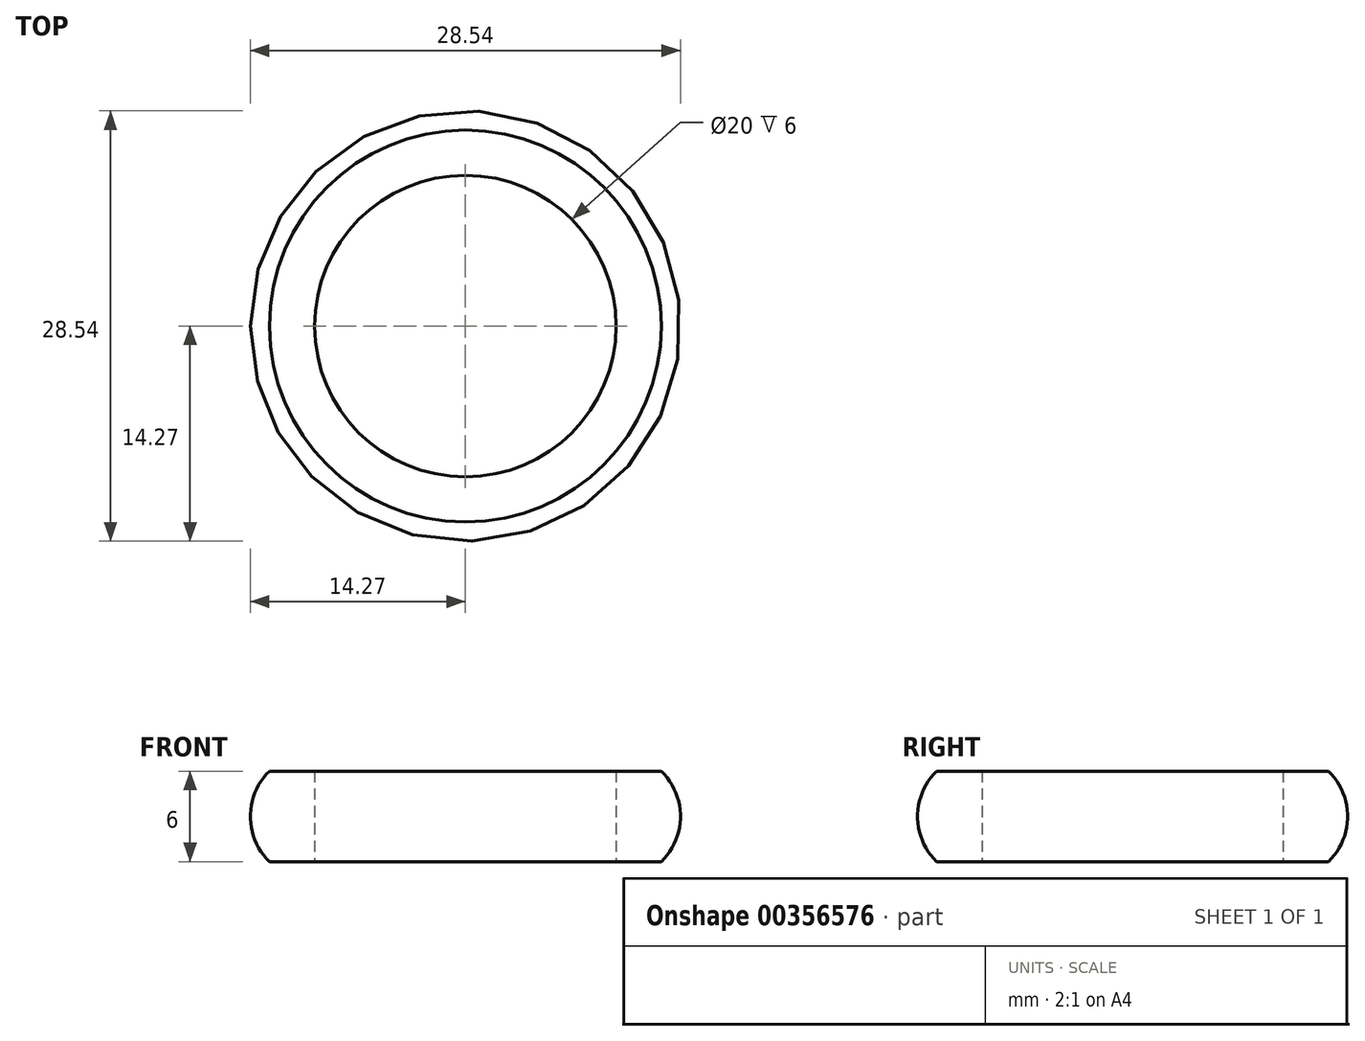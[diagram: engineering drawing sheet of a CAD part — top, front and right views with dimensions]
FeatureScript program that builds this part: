
annotation { "Feature Type Name" : "Feature", "Feature Type Description" : "" }
export const myFeature = defineFeature(function(context is Context, id is Id, definition is map)
    precondition{}
    {
        {
            var Q0;
            Q0=qCreatedBy(makeId("Front.planeOp"),FACE);
            var sketch = newSketch(context, id + "F0", { "sketchPlane" : qUnion([Q0])});
            skLineSegment(sketch, "E0", {"start": v(0, 0) * mm, "end": v(0, 6) * mm});
            skLineSegment(sketch, "E1", {"start": v(0, 6) * mm, "end": v(-3, 6) * mm});
            skLineSegment(sketch, "E2", {"start": v(0, 0) * mm, "end": v(-3, 0) * mm});
            skArc(sketch, "E3", {"start": v(-3, 6) * mm, "mid": v(-4.27, 3) * mm, "end": v(-3, 0) * mm});
            skLineSegment(sketch, "E4.0", {"start": v(10, 0) * mm, "end": v(10, 6) * mm});
            skSolve(sketch);
        }
        {
            var Q0;
            Q0 = qSketchRegion(id + "F0", true);
            var Q1;
            Q1=sQuery(id+"F0.wireOp",EDGE,"E4.0");
            revolve(context, id + "F1", {"entities" : qUnion([Q0]), "axis" : qUnion([Q1]), "revolveType" : RevolveType.FULL});
        }
    });
